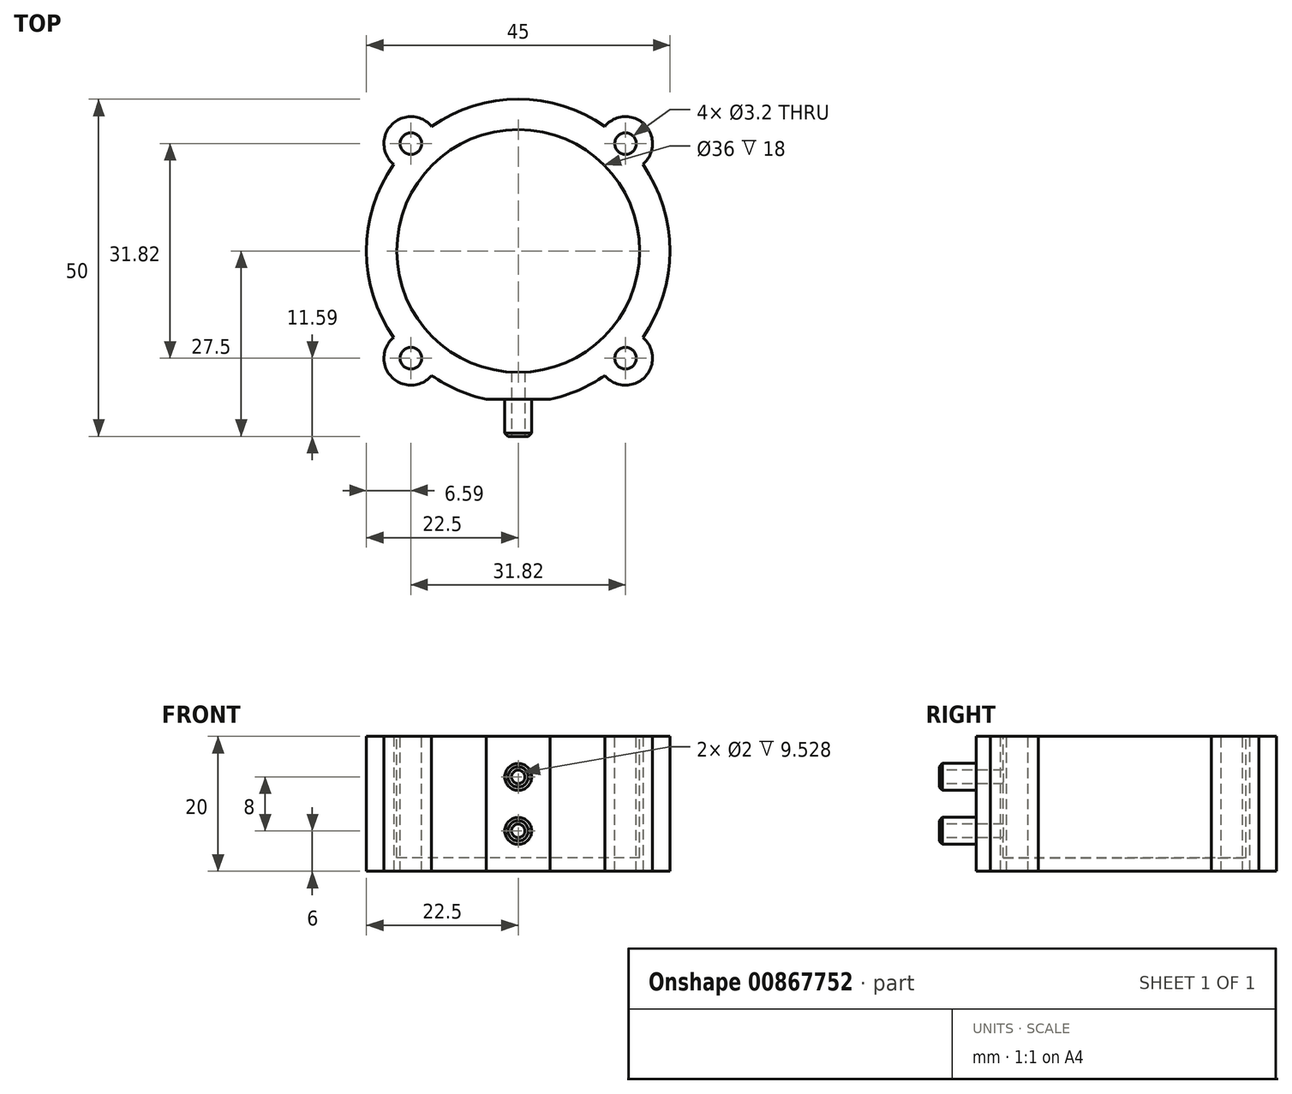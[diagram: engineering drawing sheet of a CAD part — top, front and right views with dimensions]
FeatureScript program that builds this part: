
annotation { "Feature Type Name" : "Feature", "Feature Type Description" : "" }
export const myFeature = defineFeature(function(context is Context, id is Id, definition is map)
    precondition{}
    {
        {
            var Q0;
            Q0=qCreatedBy(makeId("Top.planeOp"),FACE);
            var sketch = newSketch(context, id + "F0", { "sketchPlane" : qUnion([Q0])});
            skArc(sketch, "E0", {"start": v(12.84, 18.48) * mm, "mid": v(0, 22.5) * mm, "end": v(-12.84, 18.48) * mm});
            skLineSegment(sketch, "E1", {"start": v(0, 0) * mm, "end": v(-27.58, 27.58) * mm, "construction": true});
            skLineSegment(sketch, "E2", {"start": v(0, 0) * mm, "end": v(35.21, 35.21) * mm, "construction": true});
            skLineSegment(sketch, "E3", {"start": v(0, 0) * mm, "end": v(26.29, -26.29) * mm, "construction": true});
            skLineSegment(sketch, "E4", {"start": v(0, 0) * mm, "end": v(-25.6, -25.6) * mm, "construction": true});
            skArc(sketch, "E5", {"start": v(-12.84, 18.48) * mm, "mid": v(-18.74, 18.74) * mm, "end": v(-18.48, 12.84) * mm});
            skArc(sketch, "E6", {"start": v(18.48, 12.84) * mm, "mid": v(18.74, 18.74) * mm, "end": v(12.84, 18.48) * mm});
            skArc(sketch, "E7", {"start": v(12.84, -18.48) * mm, "mid": v(18.74, -18.74) * mm, "end": v(18.48, -12.84) * mm});
            skArc(sketch, "E8", {"start": v(-18.48, -12.84) * mm, "mid": v(-18.74, -18.74) * mm, "end": v(-12.84, -18.48) * mm});
            skArc(sketch, "E9.trimOffspring", {"start": v(-18.48, 12.84) * mm, "mid": v(-22.5, 0) * mm, "end": v(-18.48, -12.84) * mm});
            skArc(sketch, "E10.trimOffspring", {"start": v(-12.84, -18.48) * mm, "mid": v(-8.95, -20.64) * mm, "end": v(-4.72, -22) * mm});
            skArc(sketch, "E11.trimOffspring", {"start": v(18.48, -12.84) * mm, "mid": v(22.5, 0) * mm, "end": v(18.48, 12.84) * mm});
            skCircle(sketch, "E12", {"center": v(0, 0) * mm, "radius": 18.63 * mm, "construction": true});
            skLineSegment(sketch, "E13", {"start": v(-4.72, -22) * mm, "end": v(4.72, -22) * mm});
            skArc(sketch, "E14.trimOffspring", {"start": v(4.72, -22) * mm, "mid": v(8.95, -20.64) * mm, "end": v(12.84, -18.48) * mm});
            skSolve(sketch);
        }
        {
            var Q0;
            Q0 = qSketchRegion(id + "F0", true);
            extrude(context, id + "F1", {"entities" : qUnion([Q0]), "depth" : 20 * mm, "offsetDistance" : 25 * mm});
        }
        {
            var Q0;
            Q0=makeQuery(id+"F1.opExtrude","CAP_FACE",FACE,{"disambiguationData":[OSD([sQuery(id+"F0.wireOp",EDGE,"E0"),sQuery(id+"F0.wireOp",EDGE,"E5"),sQuery(id+"F0.wireOp",EDGE,"E6"),sQuery(id+"F0.wireOp",EDGE,"E7"),sQuery(id+"F0.wireOp",EDGE,"E8"),sQuery(id+"F0.wireOp",EDGE,"E9.trimOffspring"),sQuery(id+"F0.wireOp",EDGE,"E10.trimOffspring"),sQuery(id+"F0.wireOp",EDGE,"E11.trimOffspring"),sQuery(id+"F0.wireOp",EDGE,"E13"),sQuery(id+"F0.wireOp",EDGE,"E14.trimOffspring")])],"isStart":false});
            var sketch = newSketch(context, id + "F2", { "sketchPlane" : qUnion([Q0])});
            skCircle(sketch, "E15", {"center": v(-15.9, 15.9) * mm, "radius": 1.6 * mm});
            skCircle(sketch, "E16", {"center": v(15.9, 15.9) * mm, "radius": 1.6 * mm});
            skCircle(sketch, "E17", {"center": v(15.9, -15.9) * mm, "radius": 1.6 * mm});
            skCircle(sketch, "E18", {"center": v(-15.9, -15.9) * mm, "radius": 1.6 * mm});
            skSolve(sketch);
        }
        {
            var Q0;
            Q0 = qSketchRegion(id + "F2", true);
            extrude(context, id + "F3", {"entities" : qUnion([Q0]), "operationType" : NewBodyOperationType.REMOVE, "endBound" : BoundingType.THROUGH_ALL, "oppositeDirection" : true, "depth" : 25 * mm, "offsetDistance" : 25 * mm});
        }
        {
            var Q0;
            Q0=makeQuery(id+"F1.opExtrude","CAP_FACE",FACE,{"disambiguationData":[OSD([sQuery(id+"F0.wireOp",EDGE,"E0"),sQuery(id+"F0.wireOp",EDGE,"E5"),sQuery(id+"F0.wireOp",EDGE,"E6"),sQuery(id+"F0.wireOp",EDGE,"E7"),sQuery(id+"F0.wireOp",EDGE,"E8"),sQuery(id+"F0.wireOp",EDGE,"E9.trimOffspring"),sQuery(id+"F0.wireOp",EDGE,"E10.trimOffspring"),sQuery(id+"F0.wireOp",EDGE,"E11.trimOffspring"),sQuery(id+"F0.wireOp",EDGE,"E13"),sQuery(id+"F0.wireOp",EDGE,"E14.trimOffspring")])],"isStart":false});
            var sketch = newSketch(context, id + "F4", { "sketchPlane" : qUnion([Q0])});
            skCircle(sketch, "E19", {"center": v(0, 0) * mm, "radius": 18 * mm});
            skSolve(sketch);
        }
        {
            var Q0;
            Q0 = qSketchRegion(id + "F4", true);
            extrude(context, id + "F5", {"entities" : qUnion([Q0]), "operationType" : NewBodyOperationType.REMOVE, "oppositeDirection" : true, "depth" : 18 * mm, "offsetDistance" : 25 * mm});
        }
        {
            var Q0;
            Q0=makeQuery(id+"F1.opExtrude","SWEPT_FACE",FACE,{"disambiguationData":[OSD([sQuery(id+"F0.wireOp",EDGE,"E13")])]});
            var sketch = newSketch(context, id + "F6", { "sketchPlane" : qUnion([Q0])});
            skCircle(sketch, "E20", {"center": v(0, 14) * mm, "radius": 2 * mm});
            skCircle(sketch, "E21", {"center": v(0, 6) * mm, "radius": 2 * mm});
            skSolve(sketch);
        }
        {
            var Q0;
            Q0 = qSketchRegion(id + "F6", true);
            extrude(context, id + "F7", {"entities" : qUnion([Q0]), "operationType" : NewBodyOperationType.ADD, "depth" : 5.5 * mm, "offsetDistance" : 25 * mm});
        }
        {
            var Q0;
            Q0=makeQuery(id+"F7.opExtrude","CAP_FACE",FACE,{"disambiguationData":[OSD([sQuery(id+"F6.wireOp",EDGE,"E20")])],"isStart":false});
            var sketch = newSketch(context, id + "F8", { "sketchPlane" : qUnion([Q0])});
            skSolve(sketch);
        }
        {
            var Q0;
            Q0=makeQuery(id+"F7.opExtrude","CAP_FACE",FACE,{"disambiguationData":[OSD([sQuery(id+"F6.wireOp",EDGE,"E21")])],"isStart":false});
            var sketch = newSketch(context, id + "F9", { "sketchPlane" : qUnion([Q0])});
            skCircle(sketch, "E22", {"center": v(0, 6) * mm, "radius": 1 * mm});
            skSolve(sketch);
        }
        {
            var Q0;
            Q0 = qSketchRegion(id + "F9", true);
            extrude(context, id + "F10", {"entities" : qUnion([Q0]), "operationType" : NewBodyOperationType.REMOVE, "oppositeDirection" : true, "depth" : 25 * mm, "offsetDistance" : 25 * mm});
        }
        {
            var Q0;
            Q0=makeQuery(id+"F8.imprint","IMPRINT",FACE,{"disambiguationData":[TD([[makeQuery(id+"F8.imprint","IMPRINT",EDGE,{"derivedFrom":makeQuery(id+"F7.opExtrude","CAP_EDGE",EDGE,{"disambiguationData":[OSD([sQuery(id+"F6.wireOp",EDGE,"E20")])],"isStart":false})}),1.0]])]});
            var sketch = newSketch(context, id + "F11", { "sketchPlane" : qUnion([Q0])});
            skCircle(sketch, "E23", {"center": v(0, 14) * mm, "radius": 1 * mm});
            skSolve(sketch);
        }
        {
            var Q0;
            Q0 = qSketchRegion(id + "F11", true);
            extrude(context, id + "F12", {"entities" : qUnion([Q0]), "operationType" : NewBodyOperationType.REMOVE, "oppositeDirection" : true, "depth" : 25 * mm, "offsetDistance" : 25 * mm});
        }
        {
            var Q0;
            Q0=makeQuery(id+"F7.opExtrude","CAP_EDGE",EDGE,{"disambiguationData":[OSD([sQuery(id+"F6.wireOp",EDGE,"E20")])],"isStart":false});
            var Q1;
            Q1=makeQuery(id+"F7.opExtrude","CAP_EDGE",EDGE,{"disambiguationData":[OSD([sQuery(id+"F6.wireOp",EDGE,"E21")])],"isStart":false});
            chamfer(context, id + "F13", {"entities" : qUnion([Q0, Q1]), "width" : 0.5 * mm, "tangentPropagation" : true});
        }
    });
